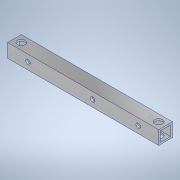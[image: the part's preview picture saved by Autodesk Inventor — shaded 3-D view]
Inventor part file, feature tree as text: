
AUTODESK INVENTOR PART (.ipt)
format: ipt  version: 2020.3 (Build 243373000, 373)  size: 142,336 bytes
history: native  units: mm
features: sketch x4, hole x3, other x1, extrude x1
ambient origin geometry x8: Origin, YZ Plane, XZ Plane, XY Plane, X Axis, Y Axis, Z Axis, Center Point
bodies: Body1 (feature_tree)
feature tree (9):
  other  "ソリッド1"
  extrude  "押し出し1"  Depth=9.0mm
  hole  "穴1"  [1 undecoded]
  hole  "穴2"  [1 undecoded]
  hole  "穴3"  [1 undecoded]
  sketch  "スケッチ1"
  sketch  "スケッチ2"
  sketch  "スケッチ3"
  sketch  "スケッチ4"
note: 3 required parameter values undecoded (feature->parameter linkage not recoverable at this tier; creation-order binding heuristic only, values carry confidence <= 0.55)
